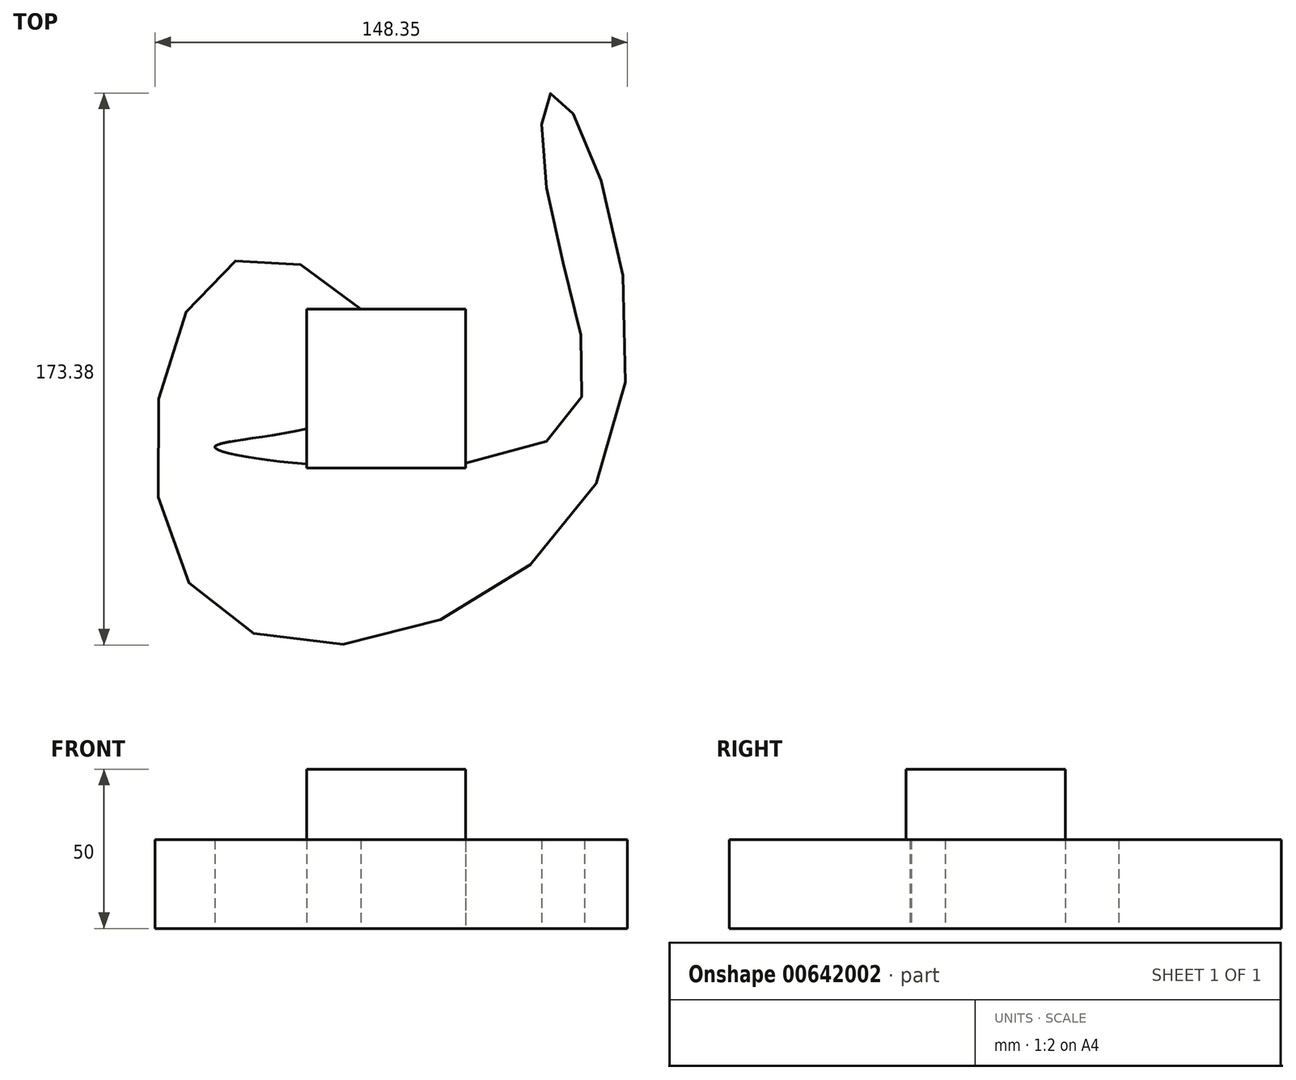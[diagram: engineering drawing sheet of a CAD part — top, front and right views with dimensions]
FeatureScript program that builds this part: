
annotation { "Feature Type Name" : "Feature", "Feature Type Description" : "" }
export const myFeature = defineFeature(function(context is Context, id is Id, definition is map)
    precondition{}
    {
        {
            var Q0;
            Q0=qCreatedBy(makeId("Top.planeOp"),FACE);
            var sketch = newSketch(context, id + "F0", { "sketchPlane" : qUnion([Q0])});
            skLineSegment(sketch, "E0.bottom", {"start": v(25, -25) * mm, "end": v(-25, -25) * mm});
            skLineSegment(sketch, "E0.top", {"start": v(25, 25) * mm, "end": v(-25, 25) * mm});
            skLineSegment(sketch, "E0.left", {"start": v(25, -25) * mm, "end": v(25, 25) * mm});
            skLineSegment(sketch, "E0.right", {"start": v(-25, -25) * mm, "end": v(-25, 25) * mm});
            skPoint(sketch, "E0.middle", {"position": v(0, 0) * mm});
            skSolve(sketch);
        }
        {
            var Q0;
            Q0 = qSketchRegion(id + "Fa1h005UuJu6Xd0_0", true);
            var Q1;
            Q1=makeQuery(id+"F0.imprint","IMPRINT",FACE,{"disambiguationData":[TD([[makeQuery(id+"F0.imprint","IMPRINT",EDGE,{"derivedFrom":sQuery(id+"F0.wireOp",EDGE,"E0.bottom")}),-1.0]])]});
            extrude(context, id + "F1", {"entities" : qUnion([Q0, Q1]), "depth" : 50 * mm, "offsetDistance" : 25 * mm});
        }
        {
            var Q0;
            Q0=qCreatedBy(makeId("Top.planeOp"),FACE);
            var sketch = newSketch(context, id + "F2", { "sketchPlane" : qUnion([Q0])});
            skFitSpline(sketch, "E1", {"points": [v(52.32, 52.32) * mm, v(50.88, -16.24) * mm, v(-53.77, -18.22) * mm, v(0, 0) * mm, v(-44.38, 41.11) * mm, v(-57.66, -66.4) * mm, v(67.84, -26.06) * mm, v(52.9, 92.74) * mm, v(52.32, 52.32) * mm]});
            skSolve(sketch);
        }
        {
            var Q0;
            Q0 = qSketchRegion(id + "F2", true);
            extrude(context, id + "F3", {"entities" : qUnion([Q0]), "operationType" : NewBodyOperationType.ADD, "depth" : 27.86 * mm, "offsetDistance" : 25 * mm});
        }
    });
